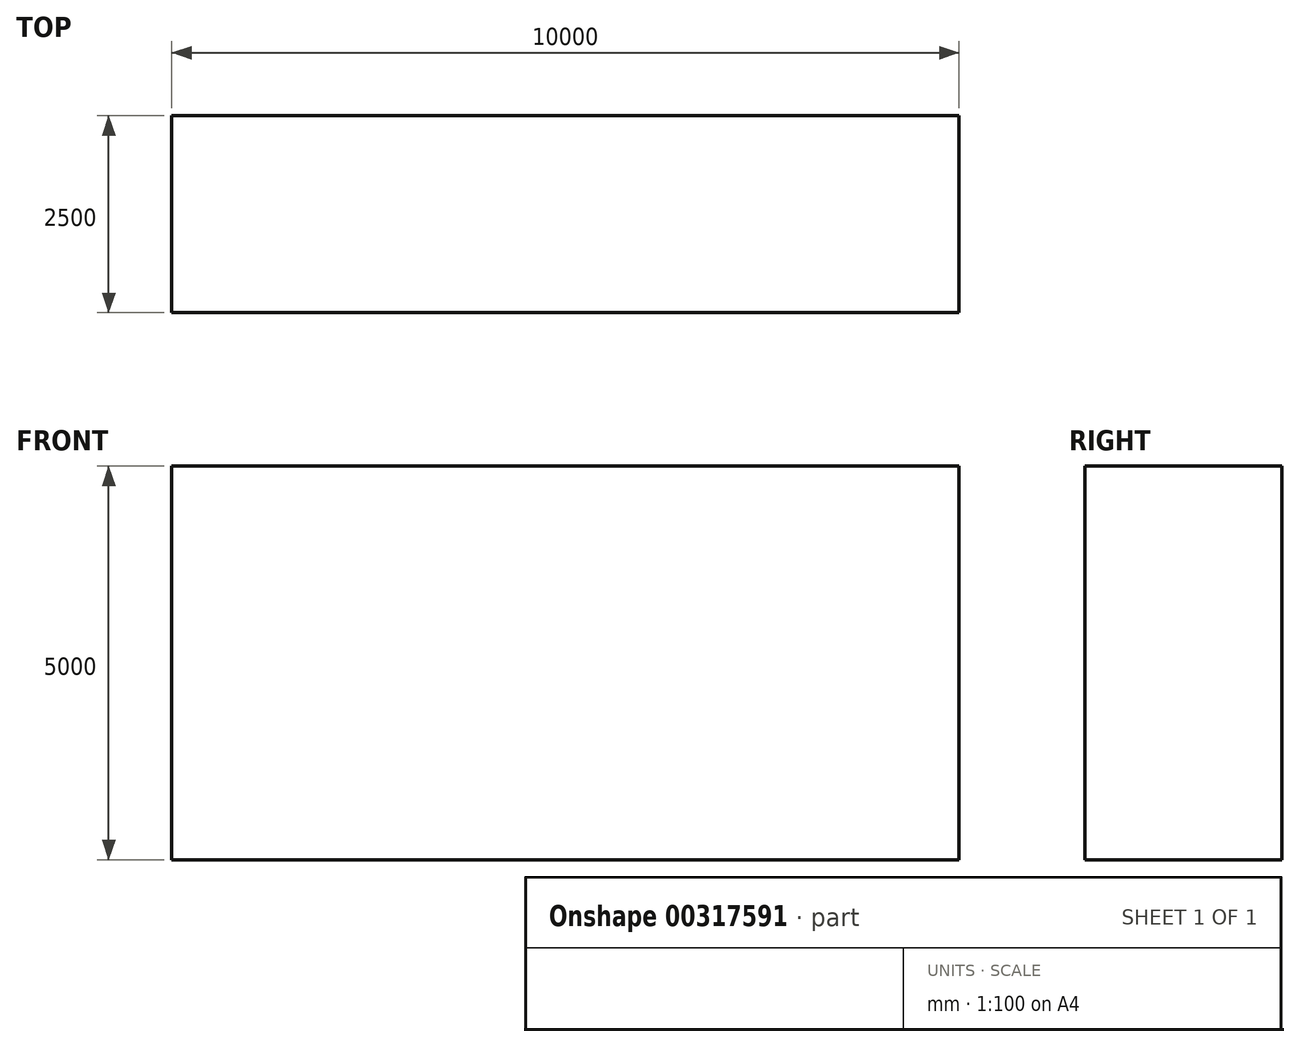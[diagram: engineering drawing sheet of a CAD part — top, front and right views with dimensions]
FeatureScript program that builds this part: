
annotation { "Feature Type Name" : "Feature", "Feature Type Description" : "" }
export const myFeature = defineFeature(function(context is Context, id is Id, definition is map)
    precondition{}
    {
        {
            var Q0;
            Q0=qCreatedBy(makeId("Front.planeOp"),FACE);
            var sketch = newSketch(context, id + "F0", { "sketchPlane" : qUnion([Q0])});
            skLineSegment(sketch, "E0.bottom", {"start": v(6615.38, 2499.72) * mm, "end": v(-3384.62, 2499.72) * mm});
            skLineSegment(sketch, "E0.top", {"start": v(6615.38, -2500.28) * mm, "end": v(-3384.62, -2500.28) * mm});
            skLineSegment(sketch, "E0.left", {"start": v(6615.38, 2499.72) * mm, "end": v(6615.38, -2500.28) * mm});
            skLineSegment(sketch, "E0.right", {"start": v(-3384.62, 2499.72) * mm, "end": v(-3384.62, -2500.28) * mm});
            skSolve(sketch);
        }
        {
            var Q0;
            Q0 = qSketchRegion(id + "F0", true);
            extrude(context, id + "F1", {"entities" : qUnion([Q0]), "depth" : 2500 * mm});
        }
    });
